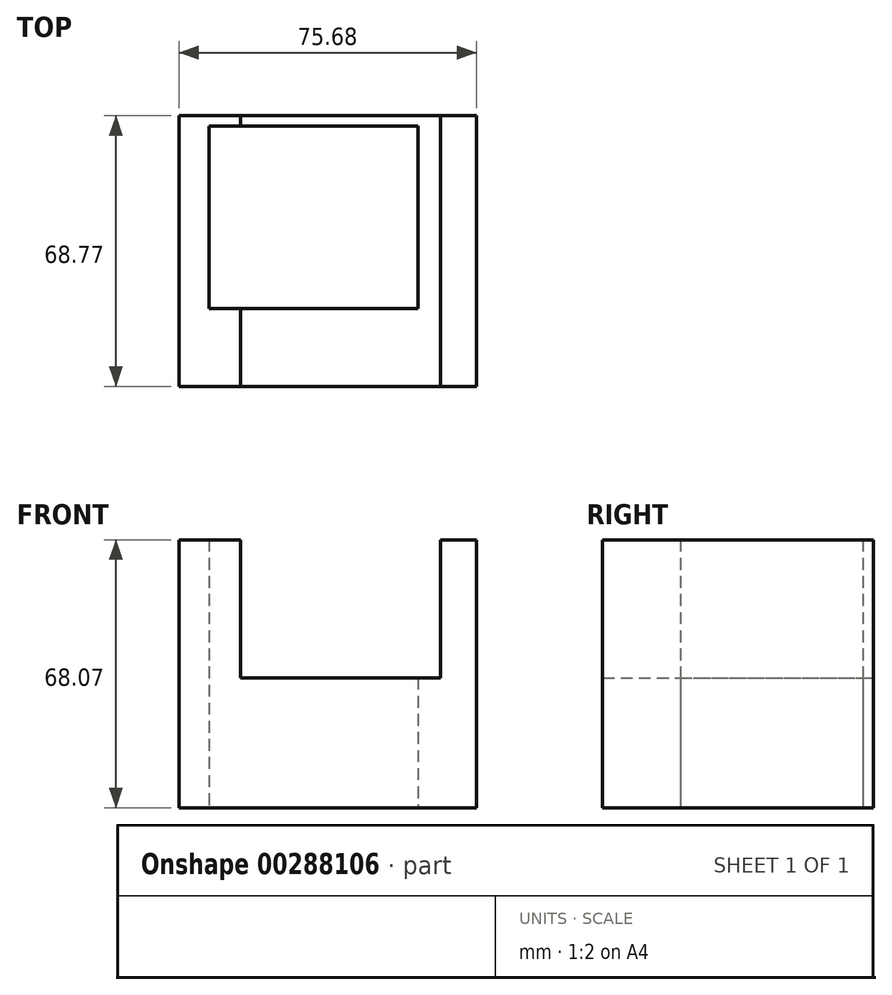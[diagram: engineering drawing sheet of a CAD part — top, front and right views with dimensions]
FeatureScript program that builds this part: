
annotation { "Feature Type Name" : "Feature", "Feature Type Description" : "" }
export const myFeature = defineFeature(function(context is Context, id is Id, definition is map)
    precondition{}
    {
        {
            var Q0;
            Q0=qCreatedBy(makeId("Top.planeOp"),FACE);
            var sketch = newSketch(context, id + "F0", { "sketchPlane" : qUnion([Q0])});
            skLineSegment(sketch, "E0.bottom", {"start": v(-41.13, 33.5) * mm, "end": v(34.55, 33.5) * mm});
            skLineSegment(sketch, "E0.top", {"start": v(-41.13, -35.27) * mm, "end": v(34.55, -35.27) * mm});
            skLineSegment(sketch, "E0.left", {"start": v(-41.13, 33.5) * mm, "end": v(-41.13, -35.27) * mm});
            skLineSegment(sketch, "E0.right", {"start": v(34.55, 33.5) * mm, "end": v(34.55, -35.27) * mm});
            skSolve(sketch);
        }
        {
            var Q0;
            Q0 = qSketchRegion(id + "F0", true);
            extrude(context, id + "F1", {"entities" : qUnion([Q0]), "depth" : 68.07 * mm});
        }
        {
            var Q0;
            Q0=qCreatedBy(makeId("Top.planeOp"),FACE);
            var sketch = newSketch(context, id + "F2", { "sketchPlane" : qUnion([Q0])});
            skLineSegment(sketch, "E1.bottom", {"start": v(-33.5, 30.81) * mm, "end": v(19.6, 30.81) * mm});
            skLineSegment(sketch, "E1.top", {"start": v(-33.5, -15.53) * mm, "end": v(19.6, -15.53) * mm});
            skLineSegment(sketch, "E1.left", {"start": v(-33.5, 30.81) * mm, "end": v(-33.5, -15.53) * mm});
            skLineSegment(sketch, "E1.right", {"start": v(19.6, 30.81) * mm, "end": v(19.6, -15.53) * mm});
            skSolve(sketch);
        }
        {
            var Q0;
            Q0 = qSketchRegion(id + "F2", true);
            extrude(context, id + "F3", {"entities" : qUnion([Q0]), "operationType" : NewBodyOperationType.REMOVE, "depth" : 104.9 * mm});
        }
        {
            var Q0;
            Q0=qCreatedBy(makeId("Right.planeOp"),FACE);
            var sketch = newSketch(context, id + "F4", { "sketchPlane" : qUnion([Q0])});
            skLineSegment(sketch, "E2.bottom", {"start": v(-54.4, 33.03) * mm, "end": v(83.36, 33.03) * mm});
            skLineSegment(sketch, "E2.top", {"start": v(-54.4, 100.93) * mm, "end": v(83.36, 100.93) * mm});
            skLineSegment(sketch, "E2.left", {"start": v(-54.4, 33.03) * mm, "end": v(-54.4, 100.93) * mm});
            skLineSegment(sketch, "E2.right", {"start": v(83.36, 33.03) * mm, "end": v(83.36, 100.93) * mm});
            skSolve(sketch);
        }
        {
            var Q0;
            Q0 = qSketchRegion(id + "F4", true);
            extrude(context, id + "F5", {"entities" : qUnion([Q0]), "operationType" : NewBodyOperationType.REMOVE, "endBound" : BoundingType.SYMMETRIC, "oppositeDirection" : true, "depth" : 50.8 * mm});
        }
    });
